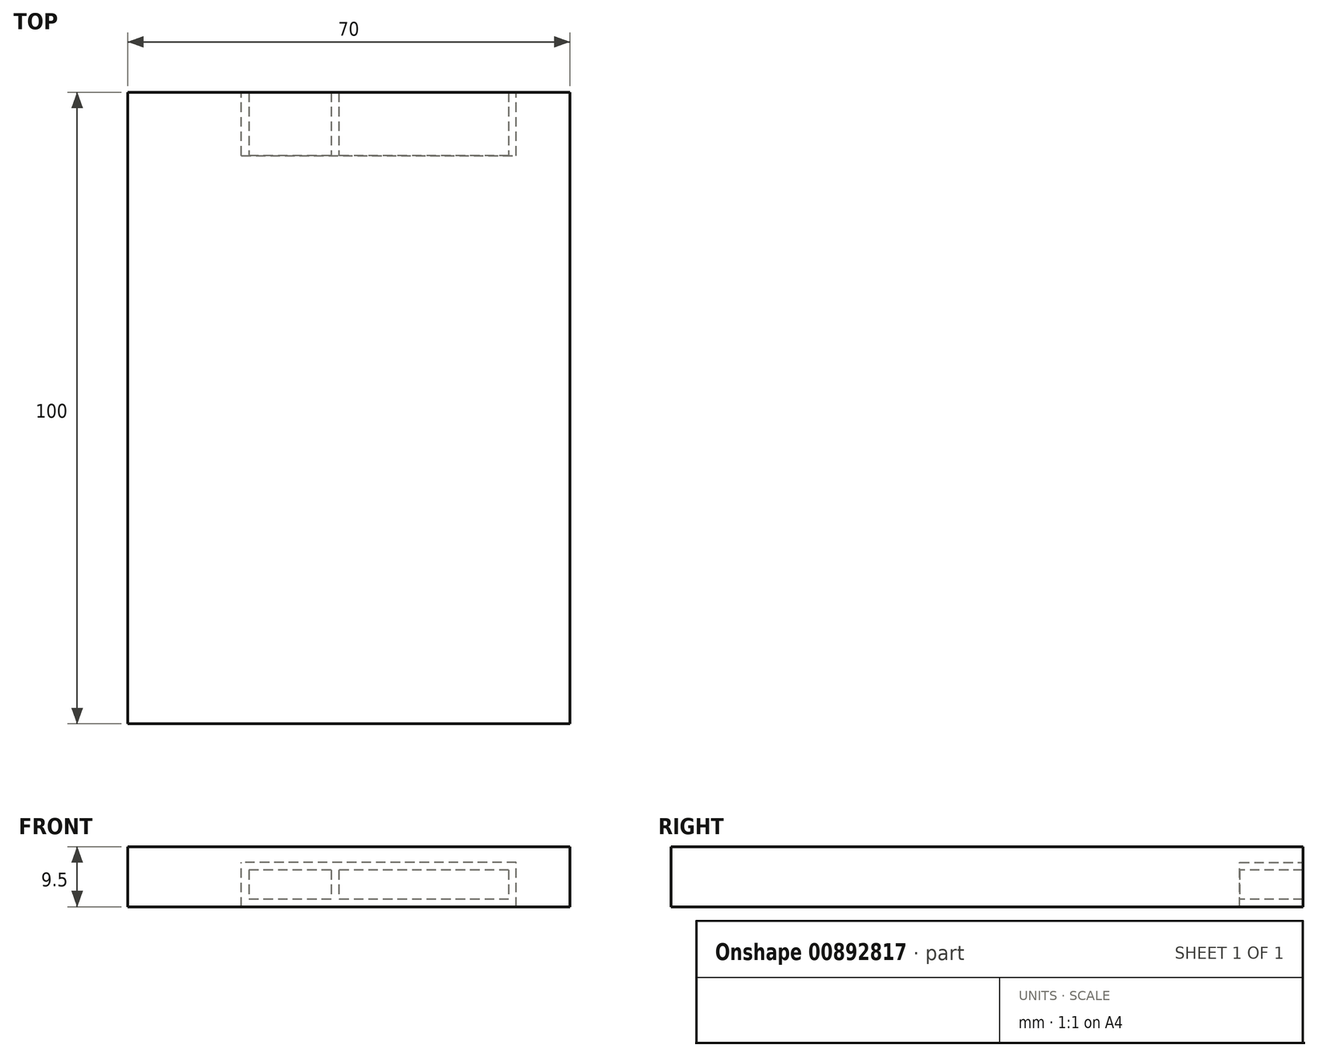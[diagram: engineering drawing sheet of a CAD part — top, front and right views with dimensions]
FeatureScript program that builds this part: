
annotation { "Feature Type Name" : "Feature", "Feature Type Description" : "" }
export const myFeature = defineFeature(function(context is Context, id is Id, definition is map)
    precondition{}
    {
        {
            var Q0;
            Q0=qCreatedBy(makeId("Top.planeOp"),FACE);
            var sketch = newSketch(context, id + "F0", { "sketchPlane" : qUnion([Q0])});
            skLineSegment(sketch, "E0.bottom", {"start": v(-35, 50) * mm, "end": v(35, 50) * mm});
            skLineSegment(sketch, "E0.top", {"start": v(-35, -50) * mm, "end": v(35, -50) * mm});
            skLineSegment(sketch, "E0.left", {"start": v(-35, 50) * mm, "end": v(-35, -50) * mm});
            skLineSegment(sketch, "E0.right", {"start": v(35, 50) * mm, "end": v(35, -50) * mm});
            skPoint(sketch, "E0.middle", {"position": v(0, 0) * mm});
            skSolve(sketch);
        }
        {
            var Q0;
            Q0=makeQuery(id+"F0.imprint","IMPRINT",FACE,{"disambiguationData":[TD([[makeQuery(id+"F0.imprint","IMPRINT",EDGE,{"derivedFrom":sQuery(id+"F0.wireOp",EDGE,"E0.bottom")}),-1.0]])]});
            extrude(context, id + "F1", {"entities" : qUnion([Q0]), "depth" : 9.5 * mm, "offsetDistance" : 25 * mm});
        }
        {
            var Q0;
            Q0=makeQuery(id+"F1.opExtrude","SWEPT_FACE",FACE,{"disambiguationData":[OSD([sQuery(id+"F0.wireOp",EDGE,"E0.bottom")])]});
            var sketch = newSketch(context, id + "F2", { "sketchPlane" : qUnion([Q0])});
            skLineSegment(sketch, "E1.bottom", {"start": v(-26.5, 0) * mm, "end": v(17, 0) * mm});
            skLineSegment(sketch, "E1.top", {"start": v(-26.5, 7) * mm, "end": v(17, 7) * mm});
            skLineSegment(sketch, "E1.left", {"start": v(-26.5, 0) * mm, "end": v(-26.5, 7) * mm});
            skLineSegment(sketch, "E1.right", {"start": v(17, 0) * mm, "end": v(17, 7) * mm});
            skSolve(sketch);
        }
        {
            var Q0;
            Q0=makeQuery(id+"F2.imprint","IMPRINT",FACE,{"disambiguationData":[TD([[makeQuery(id+"F2.imprint","IMPRINT",EDGE,{"derivedFrom":sQuery(id+"F2.wireOp",EDGE,"E1.bottom")}),-1.0]])]});
            extrude(context, id + "F3", {"entities" : qUnion([Q0]), "operationType" : NewBodyOperationType.REMOVE, "oppositeDirection" : true, "depth" : 10 * mm, "offsetDistance" : 25 * mm});
        }
        {
            var Q0;
            Q0=makeQuery(id+"F3.boolean.opBoolean","COPY",FACE,{"derivedFrom":makeQuery(id+"F3.opExtrude","CAP_FACE",FACE,{"disambiguationData":[OSD([sQuery(id+"F2.wireOp",EDGE,"E1.bottom"),sQuery(id+"F2.wireOp",EDGE,"E1.top"),sQuery(id+"F2.wireOp",EDGE,"E1.left"),sQuery(id+"F2.wireOp",EDGE,"E1.right")])],"isStart":false})});
            var sketch = newSketch(context, id + "F4", { "sketchPlane" : qUnion([Q0])});
            skLineSegment(sketch, "E2.bottom", {"start": v(-25.3, 5.8) * mm, "end": v(1.6, 5.8) * mm});
            skLineSegment(sketch, "E2.top", {"start": v(-25.3, 1.2) * mm, "end": v(1.6, 1.2) * mm});
            skLineSegment(sketch, "E2.left", {"start": v(-25.3, 5.8) * mm, "end": v(-25.3, 1.2) * mm});
            skLineSegment(sketch, "E2.right", {"start": v(1.6, 5.8) * mm, "end": v(1.6, 1.2) * mm});
            skLineSegment(sketch, "E3.bottom", {"start": v(2.8, 5.8) * mm, "end": v(15.8, 5.8) * mm});
            skLineSegment(sketch, "E3.top", {"start": v(2.8, 1.2) * mm, "end": v(15.8, 1.2) * mm});
            skLineSegment(sketch, "E3.left", {"start": v(2.8, 5.8) * mm, "end": v(2.8, 1.2) * mm});
            skLineSegment(sketch, "E3.right", {"start": v(15.8, 5.8) * mm, "end": v(15.8, 1.2) * mm});
            skSolve(sketch);
        }
        {
            var Q0;
            Q0=makeQuery(id+"F4.imprint","IMPRINT",FACE,{"disambiguationData":[TD([[makeQuery(id+"F4.imprint","IMPRINT",EDGE,{"derivedFrom":sQuery(id+"F4.wireOp",EDGE,"E2.bottom")}),-1.0]])]});
            var Q1;
            Q1=makeQuery(id+"F4.imprint","IMPRINT",FACE,{"disambiguationData":[TD([[makeQuery(id+"F4.imprint","IMPRINT",EDGE,{"derivedFrom":sQuery(id+"F4.wireOp",EDGE,"E3.bottom")}),-1.0]])]});
            extrude(context, id + "F5", {"entities" : qUnion([Q0, Q1]), "operationType" : NewBodyOperationType.ADD, "depth" : 10 * mm, "offsetDistance" : 25 * mm});
        }
    });
